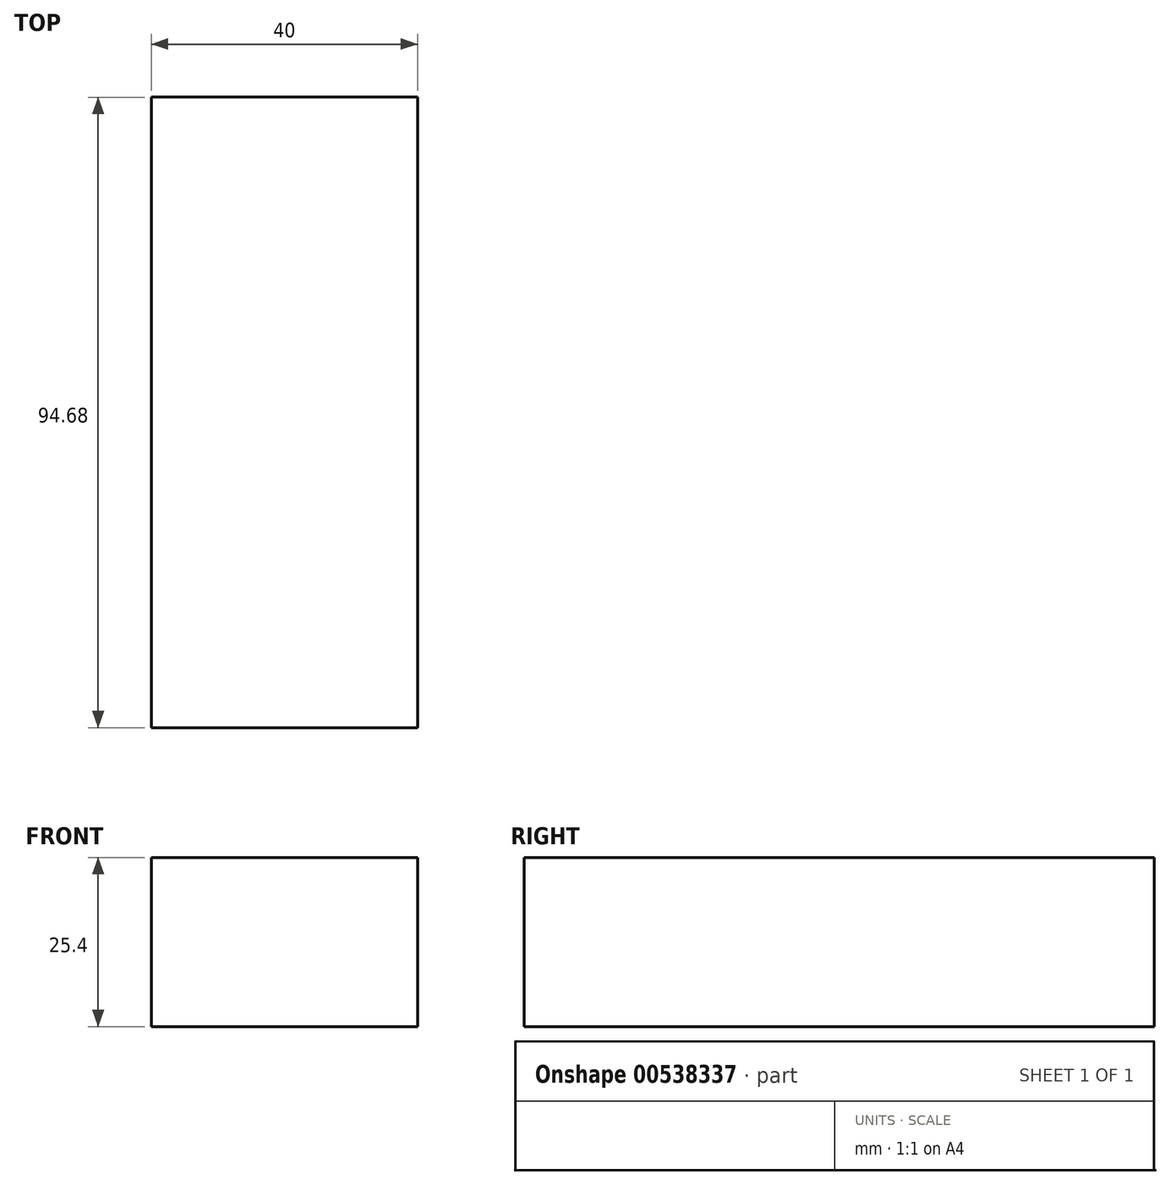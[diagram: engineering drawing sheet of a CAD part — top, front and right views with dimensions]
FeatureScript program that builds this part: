
annotation { "Feature Type Name" : "Feature", "Feature Type Description" : "" }
export const myFeature = defineFeature(function(context is Context, id is Id, definition is map)
    precondition{}
    {
        {
            var Q0;
            Q0=qCreatedBy(makeId("Top.planeOp"),FACE);
            var sketch = newSketch(context, id + "F0", { "sketchPlane" : qUnion([Q0])});
            skLineSegment(sketch, "E0.bottom", {"start": v(0, 0) * mm, "end": v(40, 0) * mm});
            skLineSegment(sketch, "E0.top", {"start": v(0, 94.68) * mm, "end": v(40, 94.68) * mm});
            skLineSegment(sketch, "E0.left", {"start": v(0, 0) * mm, "end": v(0, 94.68) * mm});
            skLineSegment(sketch, "E0.right", {"start": v(40, 0) * mm, "end": v(40, 94.68) * mm});
            skSolve(sketch);
        }
        {
            var Q0;
            Q0=makeQuery(id+"F0.imprint","IMPRINT",FACE,{"disambiguationData":[TD([[makeQuery(id+"F0.imprint","IMPRINT",EDGE,{"derivedFrom":sQuery(id+"F0.wireOp",EDGE,"E0.bottom")}),1.0]])]});
            extrude(context, id + "F1", {"entities" : qUnion([Q0]), "depth" : 25.4 * mm, "offsetDistance" : 25.4 * mm});
        }
    });
